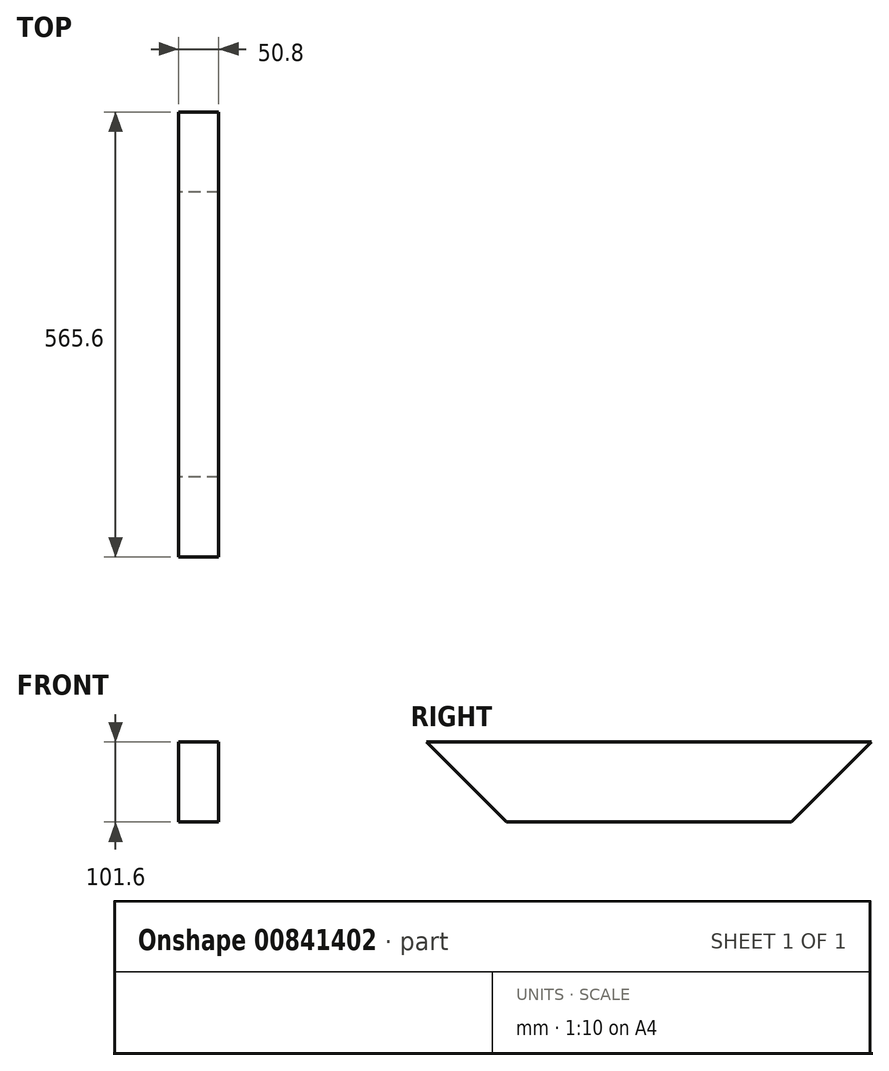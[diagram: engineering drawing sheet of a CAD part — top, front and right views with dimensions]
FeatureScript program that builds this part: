
annotation { "Feature Type Name" : "Feature", "Feature Type Description" : "" }
export const myFeature = defineFeature(function(context is Context, id is Id, definition is map)
    precondition{}
    {
        {
            var Q0;
            Q0=qCreatedBy(makeId("Right.planeOp"),FACE);
            var sketch = newSketch(context, id + "F0", { "sketchPlane" : qUnion([Q0])});
            skLineSegment(sketch, "E0.bottom", {"start": v(108.6, 50.8) * mm, "end": v(-457, 50.8) * mm});
            skLineSegment(sketch, "E0.top", {"start": v(7, -50.8) * mm, "end": v(-355.4, -50.8) * mm});
            skPoint(sketch, "E0.middle", {"position": v(0, 0) * mm});
            skLineSegment(sketch, "E1", {"start": v(-457, 50.8) * mm, "end": v(-355.4, -50.8) * mm});
            skPoint(sketch, "E2.orphan", {"position": v(-108.6, -50.8) * mm});
            skLineSegment(sketch, "E3", {"start": v(108.6, 50.8) * mm, "end": v(7, -50.8) * mm});
            skPoint(sketch, "E0.left.end.orphan", {"position": v(457, -50.8) * mm});
            skSolve(sketch);
        }
        {
            var Q0;
            Q0=makeQuery(id+"F0.imprint","IMPRINT",FACE,{"disambiguationData":[TD([[makeQuery(id+"F0.imprint","IMPRINT",EDGE,{"derivedFrom":sQuery(id+"F0.wireOp",EDGE,"E0.bottom")}),1.0]])]});
            extrude(context, id + "F1", {"entities" : qUnion([Q0]), "depth" : 50.8 * mm, "offsetDistance" : 25 * mm});
        }
    });
